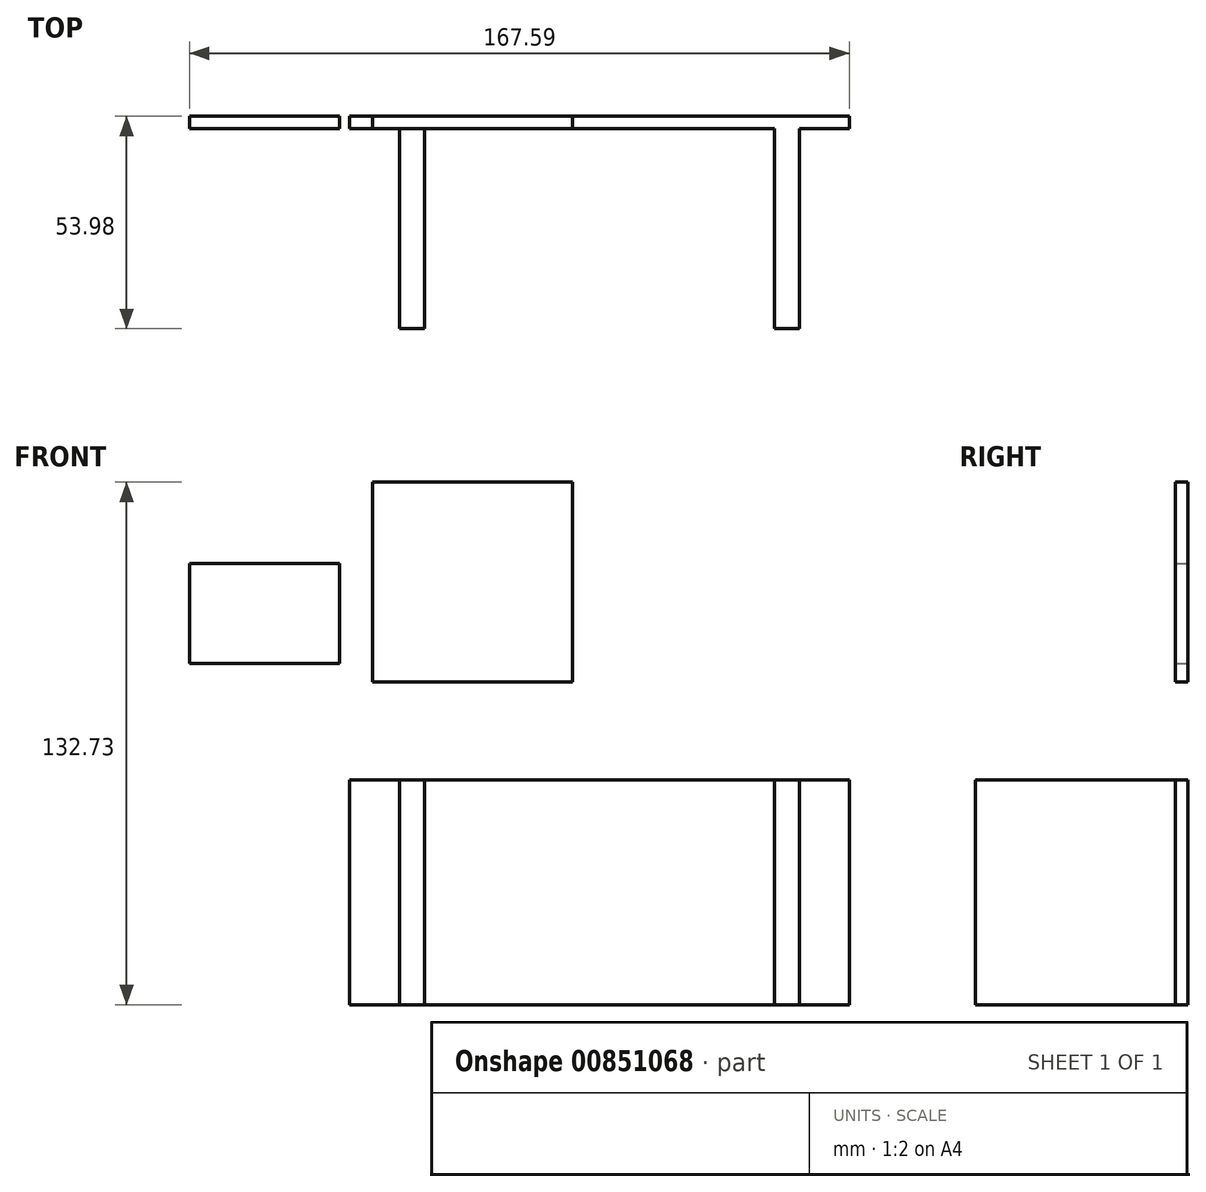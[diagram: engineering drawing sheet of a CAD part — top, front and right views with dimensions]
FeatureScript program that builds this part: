
annotation { "Feature Type Name" : "Feature", "Feature Type Description" : "" }
export const myFeature = defineFeature(function(context is Context, id is Id, definition is map)
    precondition{}
    {
        {
            var Q0;
            Q0=qCreatedBy(makeId("Front.planeOp"),FACE);
            var sketch = newSketch(context, id + "F0", { "sketchPlane" : qUnion([Q0])});
            skLineSegment(sketch, "E0.bottom", {"start": v(-27.4, 64.87) * mm, "end": v(23.4, 64.87) * mm});
            skLineSegment(sketch, "E0.top", {"start": v(-27.4, 14.07) * mm, "end": v(23.4, 14.07) * mm});
            skLineSegment(sketch, "E0.left", {"start": v(-27.4, 64.87) * mm, "end": v(-27.4, 14.07) * mm});
            skLineSegment(sketch, "E0.right", {"start": v(23.4, 64.87) * mm, "end": v(23.4, 14.07) * mm});
            skLineSegment(sketch, "E1.bottom", {"start": v(-33.22, -10.71) * mm, "end": v(93.78, -10.71) * mm});
            skLineSegment(sketch, "E1.top", {"start": v(-33.22, -67.86) * mm, "end": v(93.78, -67.86) * mm});
            skLineSegment(sketch, "E1.left", {"start": v(-33.22, -10.71) * mm, "end": v(-33.22, -67.86) * mm});
            skLineSegment(sketch, "E1.right", {"start": v(93.78, -10.71) * mm, "end": v(93.78, -67.86) * mm});
            skLineSegment(sketch, "E2.bottom", {"start": v(-73.81, 44.18) * mm, "end": v(-35.71, 44.18) * mm});
            skLineSegment(sketch, "E2.top", {"start": v(-73.81, 18.78) * mm, "end": v(-35.71, 18.78) * mm});
            skLineSegment(sketch, "E2.left", {"start": v(-73.81, 44.18) * mm, "end": v(-73.81, 18.78) * mm});
            skLineSegment(sketch, "E2.right", {"start": v(-35.71, 44.18) * mm, "end": v(-35.71, 18.78) * mm});
            skSolve(sketch);
        }
        {
            var Q0;
            Q0=makeQuery(id+"F0.imprint","IMPRINT",FACE,{"disambiguationData":[TD([[makeQuery(id+"F0.imprint","IMPRINT",EDGE,{"derivedFrom":sQuery(id+"F0.wireOp",EDGE,"E2.bottom")}),-1.0]])]});
            var Q1;
            Q1=makeQuery(id+"F0.imprint","IMPRINT",FACE,{"disambiguationData":[TD([[makeQuery(id+"F0.imprint","IMPRINT",EDGE,{"derivedFrom":sQuery(id+"F0.wireOp",EDGE,"E0.bottom")}),-1.0]])]});
            var Q2;
            Q2=makeQuery(id+"F0.imprint","IMPRINT",FACE,{"disambiguationData":[TD([[makeQuery(id+"F0.imprint","IMPRINT",EDGE,{"derivedFrom":sQuery(id+"F0.wireOp",EDGE,"E1.bottom")}),-1.0]])]});
            extrude(context, id + "F1", {"entities" : qUnion([Q0, Q1, Q2]), "depth" : 3.17 * mm, "offsetDistance" : 25.4 * mm});
        }
        {
            var Q0;
            Q0=makeQuery(id+"F1.opExtrude","CAP_FACE",FACE,{"disambiguationData":[OSD([sQuery(id+"F0.wireOp",EDGE,"E1.bottom"),sQuery(id+"F0.wireOp",EDGE,"E1.top"),sQuery(id+"F0.wireOp",EDGE,"E1.left"),sQuery(id+"F0.wireOp",EDGE,"E1.right")])],"isStart":false});
            var sketch = newSketch(context, id + "F2", { "sketchPlane" : qUnion([Q0])});
            skLineSegment(sketch, "E3.bottom", {"start": v(-20.52, -10.71) * mm, "end": v(-14.17, -10.71) * mm});
            skLineSegment(sketch, "E3.top", {"start": v(-20.52, -67.86) * mm, "end": v(-14.17, -67.86) * mm});
            skLineSegment(sketch, "E3.left", {"start": v(-20.52, -10.71) * mm, "end": v(-20.52, -67.86) * mm});
            skLineSegment(sketch, "E3.right", {"start": v(-14.17, -10.71) * mm, "end": v(-14.17, -67.86) * mm});
            skLineSegment(sketch, "E4.bottom", {"start": v(81.08, -10.71) * mm, "end": v(74.73, -10.71) * mm});
            skLineSegment(sketch, "E4.top", {"start": v(81.08, -67.86) * mm, "end": v(74.73, -67.86) * mm});
            skLineSegment(sketch, "E4.left", {"start": v(81.08, -10.71) * mm, "end": v(81.08, -67.86) * mm});
            skLineSegment(sketch, "E4.right", {"start": v(74.73, -10.71) * mm, "end": v(74.73, -67.86) * mm});
            skSolve(sketch);
        }
        {
            var Q0;
            Q0 = qSketchRegion(id + "F2", true);
            extrude(context, id + "F3", {"entities" : qUnion([Q0]), "operationType" : NewBodyOperationType.ADD, "depth" : 50.8 * mm, "offsetDistance" : 25.4 * mm});
        }
    });
